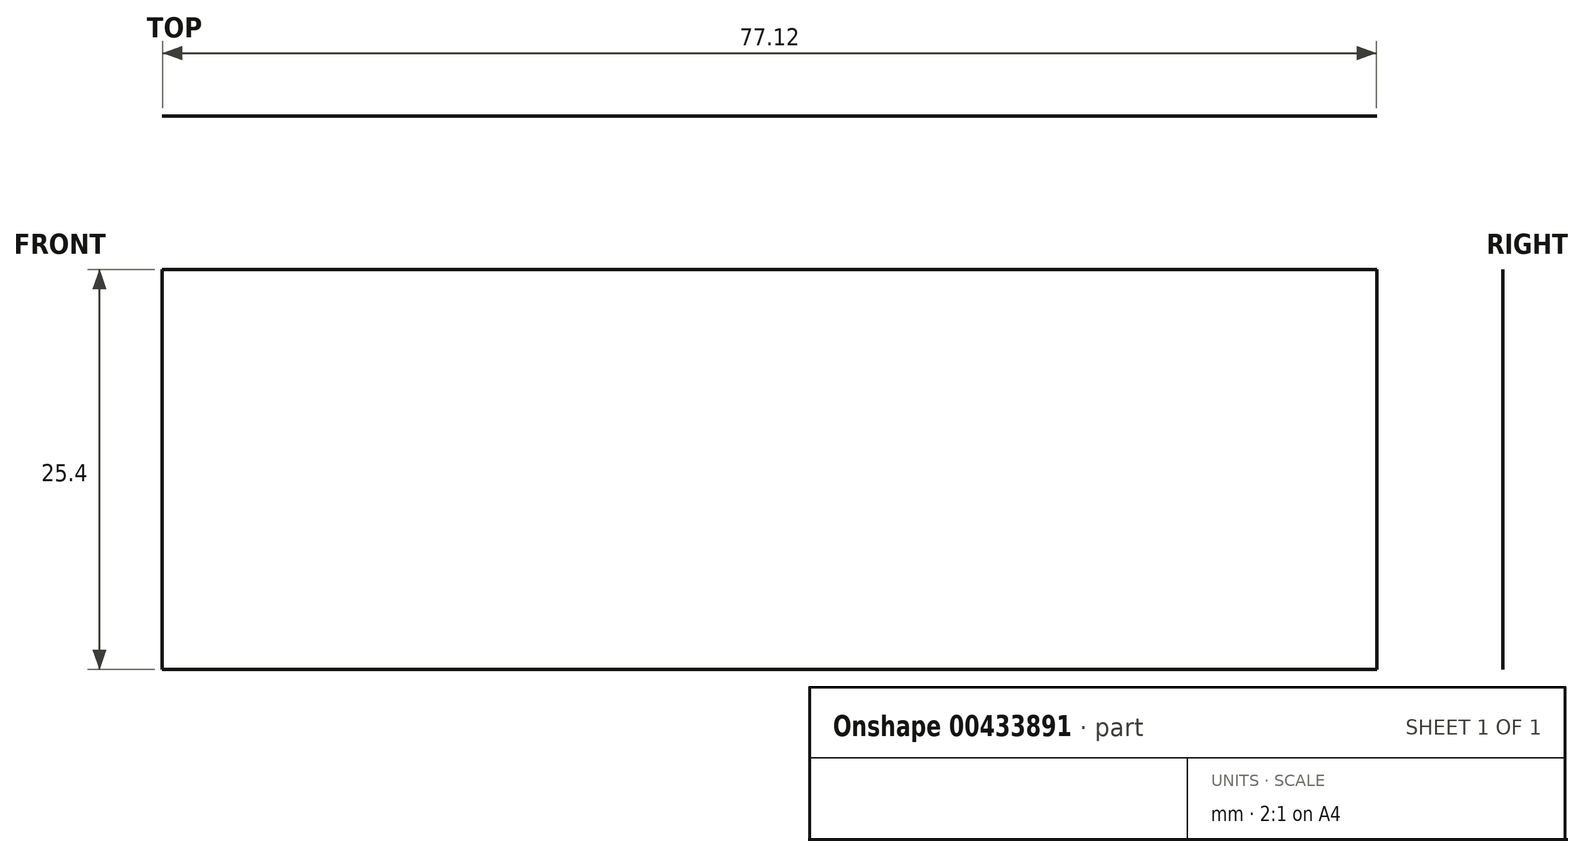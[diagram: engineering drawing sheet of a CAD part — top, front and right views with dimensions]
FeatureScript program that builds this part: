
annotation { "Feature Type Name" : "Feature", "Feature Type Description" : "" }
export const myFeature = defineFeature(function(context is Context, id is Id, definition is map)
    precondition{}
    {
        {
            var Q0;
            Q0=qCreatedBy(makeId("Top.planeOp"),FACE);
            var sketch = newSketch(context, id + "F0", { "sketchPlane" : qUnion([Q0])});
            skLineSegment(sketch, "E0.bottom", {"start": v(-26.84, 35.41) * mm, "end": v(50.28, 35.41) * mm});
            skLineSegment(sketch, "E0.top", {"start": v(-26.84, -39.66) * mm, "end": v(50.28, -39.66) * mm});
            skLineSegment(sketch, "E0.left", {"start": v(-26.84, 35.41) * mm, "end": v(-26.84, -39.66) * mm});
            skLineSegment(sketch, "E0.right", {"start": v(50.28, 35.41) * mm, "end": v(50.28, -39.66) * mm});
            skLineSegment(sketch, "E1.bottom", {"start": v(48.31, -41.94) * mm, "end": v(71.97, -41.94) * mm});
            skLineSegment(sketch, "E1.top", {"start": v(48.31, -61.18) * mm, "end": v(71.97, -61.18) * mm});
            skLineSegment(sketch, "E1.left", {"start": v(48.31, -41.94) * mm, "end": v(48.31, -61.18) * mm});
            skLineSegment(sketch, "E1.right", {"start": v(71.97, -41.94) * mm, "end": v(71.97, -61.18) * mm});
            skSolve(sketch);
        }
        {
            var Q0;
            Q0=makeQuery(id+"F0.imprint","IMPRINT",FACE,{"disambiguationData":[TD([[makeQuery(id+"F0.imprint","IMPRINT",EDGE,{"derivedFrom":sQuery(id+"F0.wireOp",EDGE,"E0.bottom")}),-1.0]])]});
            var sketch = newSketch(context, id + "F1", { "sketchPlane" : qUnion([Q0])});
            skSolve(sketch);
        }
        {
            var Q0;
            Q0 = qSketchRegion(id + "F1", true);
            var Q1;
            Q1=sQuery(id+"F0.wireOp",EDGE,"E0.bottom");
            extrude(context, id + "F2", {"entities" : qUnion([Q0]), "bodyType" : ToolBodyType.SURFACE, "surfaceEntities" : qUnion([Q1]), "depth" : 25.4 * mm});
        }
    });
